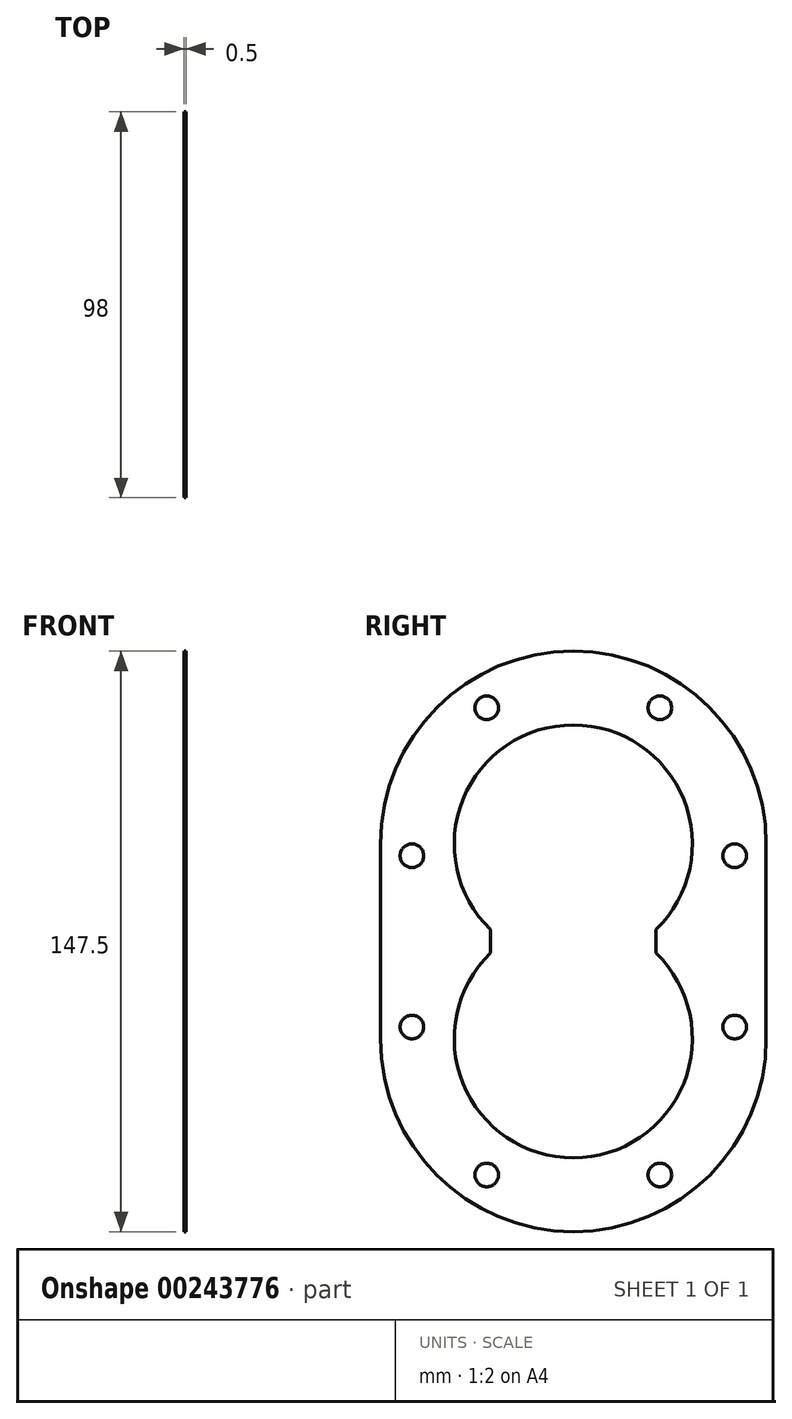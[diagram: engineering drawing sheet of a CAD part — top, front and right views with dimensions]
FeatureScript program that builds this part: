
annotation { "Feature Type Name" : "Feature", "Feature Type Description" : "" }
export const myFeature = defineFeature(function(context is Context, id is Id, definition is map)
    precondition{}
    {
        {
            var Q0;
            Q0=qCreatedBy(makeId("Right.planeOp"),FACE);
            var sketch = newSketch(context, id + "F0", { "sketchPlane" : qUnion([Q0])});
            skArc(sketch, "E0", {"start": v(49, 24.75) * mm, "mid": v(0, 73.75) * mm, "end": v(-49, 24.75) * mm});
            skArc(sketch, "E1", {"start": v(21, 2.98) * mm, "mid": v(0, 55) * mm, "end": v(-21, 2.98) * mm});
            skArc(sketch, "E2.MirrorC", {"start": v(21, -2.98) * mm, "mid": v(0, -55) * mm, "end": v(-21, -2.98) * mm});
            skArc(sketch, "E3.MirrorC", {"start": v(49, -24.75) * mm, "mid": v(0, -73.75) * mm, "end": v(-49, -24.75) * mm});
            skLineSegment(sketch, "E4", {"start": v(49, 24.75) * mm, "end": v(49, -24.75) * mm});
            skLineSegment(sketch, "E5.MirrorCS", {"start": v(-49, 24.75) * mm, "end": v(-49, -24.75) * mm});
            skLineSegment(sketch, "E6", {"start": v(21, 2.98) * mm, "end": v(21, -2.98) * mm});
            skLineSegment(sketch, "E7.MirrorCS", {"start": v(-21, 2.98) * mm, "end": v(-21, -2.98) * mm});
            skArc(sketch, "E8", {"start": v(41, 24.75) * mm, "mid": v(0, 65.75) * mm, "end": v(-41, 24.75) * mm, "construction": true});
            skArc(sketch, "E9.MirrorC", {"start": v(41, -24.75) * mm, "mid": v(0, -65.75) * mm, "end": v(-41, -24.75) * mm, "construction": true});
            skLineSegment(sketch, "E10", {"start": v(41, 24.75) * mm, "end": v(41, -24.75) * mm, "construction": true});
            skLineSegment(sketch, "E11.MirrorCS", {"start": v(-41, 24.75) * mm, "end": v(-41, -24.75) * mm, "construction": true});
            skPoint(sketch, "E12", {"position": v(22, 59.35) * mm});
            skPoint(sketch, "E13", {"position": v(-22, 59.35) * mm});
            skPoint(sketch, "E14", {"position": v(41, 21.75) * mm});
            skPoint(sketch, "E15", {"position": v(41, -21.75) * mm});
            skPoint(sketch, "E16.MirrorP", {"position": v(22, -59.35) * mm});
            skPoint(sketch, "E17.MirrorP", {"position": v(-22, -59.35) * mm});
            skPoint(sketch, "E18.MirrorP", {"position": v(-41, 21.75) * mm});
            skPoint(sketch, "E19.MirrorP", {"position": v(-41, -21.75) * mm});
            skSolve(sketch);
        }
        {
            var Q0;
            Q0 = qSketchRegion(id + "F0", true);
            extrude(context, id + "F1", {"entities" : qUnion([Q0]), "depth" : 0.5 * mm});
        }
        {
            var Q0;
            Q0=sQuery(id+"F0.wireOp",VERTEX,"E12");
            var Q1;
            Q1=sQuery(id+"F0.wireOp",VERTEX,"E13");
            var Q2;
            Q2=sQuery(id+"F0.wireOp",VERTEX,"E18.MirrorP");
            var Q3;
            Q3=sQuery(id+"F0.wireOp",VERTEX,"E19.MirrorP");
            var Q4;
            Q4=sQuery(id+"F0.wireOp",VERTEX,"E17.MirrorP");
            var Q5;
            Q5=sQuery(id+"F0.wireOp",VERTEX,"E16.MirrorP");
            var Q6;
            Q6=sQuery(id+"F0.wireOp",VERTEX,"E15");
            var Q7;
            Q7=sQuery(id+"F0.wireOp",VERTEX,"E14");
            var Q8;
            Q8=makeQuery(id+"F1.opExtrude","SWEPT_BODY",BODY,{"disambiguationData":[OSD([sQuery(id+"F0.wireOp",EDGE,"E0"),sQuery(id+"F0.wireOp",EDGE,"E1"),sQuery(id+"F0.wireOp",EDGE,"E2.MirrorC"),sQuery(id+"F0.wireOp",EDGE,"E3.MirrorC"),sQuery(id+"F0.wireOp",EDGE,"E4"),sQuery(id+"F0.wireOp",EDGE,"E5.MirrorCS"),sQuery(id+"F0.wireOp",EDGE,"E6"),sQuery(id+"F0.wireOp",EDGE,"E7.MirrorCS")])]});
            hole(context, id + "F2", {"style" : HoleStyle.SIMPLE, "endStyle" : HoleEndStyle.THROUGH, "oppositeDirection" : true, "holeDiameter" : 6 * mm, "tappedDepth" : 12 * mm, "tapClearance" : 3, "locations" : qUnion([Q0, Q1, Q2, Q3, Q4, Q5, Q6, Q7]), "scope" : qUnion([Q8])});
        }
    });
